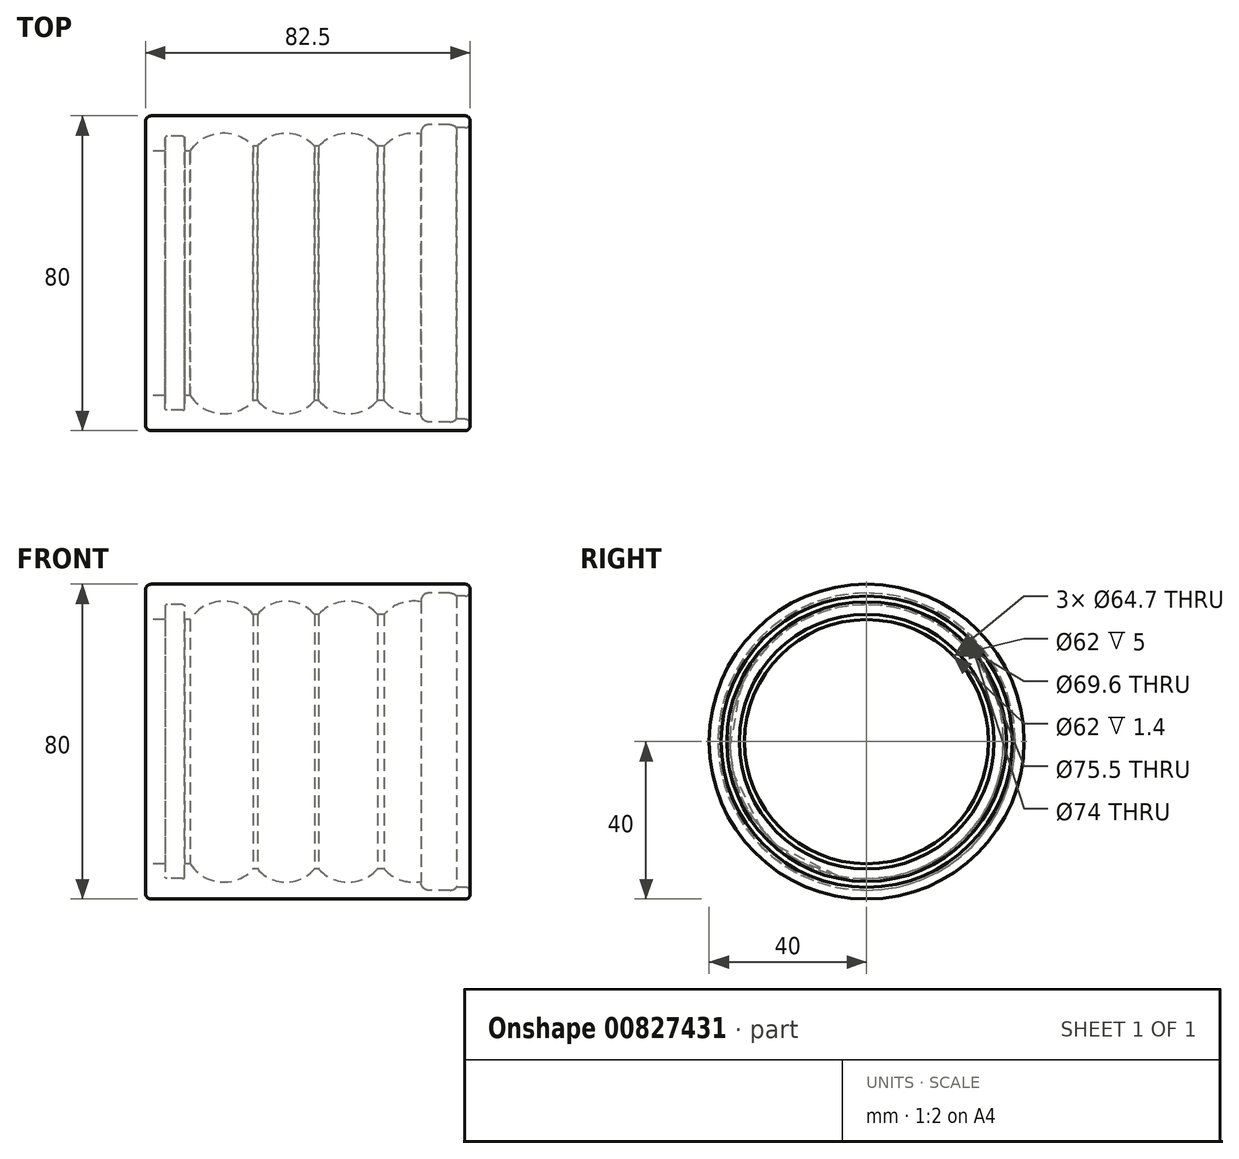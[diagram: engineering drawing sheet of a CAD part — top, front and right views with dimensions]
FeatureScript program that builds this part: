
annotation { "Feature Type Name" : "Feature", "Feature Type Description" : "" }
export const myFeature = defineFeature(function(context is Context, id is Id, definition is map)
    precondition{}
    {
        {
            var Q0;
            Q0=qCreatedBy(makeId("Front.planeOp"),FACE);
            var sketch = newSketch(context, id + "F0", { "sketchPlane" : qUnion([Q0])});
            skLineSegment(sketch, "E0", {"start": v(-106.11, 0) * mm, "end": v(111.06, 0) * mm, "construction": true});
            skLineSegment(sketch, "E1", {"start": v(82.5, 40) * mm, "end": v(0, 40) * mm});
            skLineSegment(sketch, "E2", {"start": v(0, 40) * mm, "end": v(0, 31) * mm});
            skLineSegment(sketch, "E3", {"start": v(0, 31) * mm, "end": v(5, 31) * mm});
            skLineSegment(sketch, "E4", {"start": v(5, 31) * mm, "end": v(5, 34.8) * mm});
            skLineSegment(sketch, "E5", {"start": v(5, 34.8) * mm, "end": v(10, 34.8) * mm});
            skLineSegment(sketch, "E6", {"start": v(27.35, 32.35) * mm, "end": v(28.45, 32.35) * mm});
            skLineSegment(sketch, "E7", {"start": v(70, 35.52) * mm, "end": v(70, 37.75) * mm});
            skLineSegment(sketch, "E8", {"start": v(70, 37.75) * mm, "end": v(79, 37.75) * mm});
            skLineSegment(sketch, "E9", {"start": v(79, 37.75) * mm, "end": v(79, 37) * mm});
            skLineSegment(sketch, "E10", {"start": v(79, 37) * mm, "end": v(82.5, 37) * mm});
            skPoint(sketch, "E11.start.orphan", {"position": v(82.5, 37.75) * mm});
            skLineSegment(sketch, "E12", {"start": v(82.5, 40) * mm, "end": v(82.5, 37) * mm});
            skArc(sketch, "E13", {"start": v(58.97, 32.35) * mm, "mid": v(51.5, 35.7) * mm, "end": v(44.03, 32.35) * mm});
            skArc(sketch, "E14", {"start": v(70, 35.52) * mm, "mid": v(64.92, 35.17) * mm, "end": v(60.67, 32.35) * mm});
            skLineSegment(sketch, "E15", {"start": v(10, 34.8) * mm, "end": v(10, 31) * mm});
            skLineSegment(sketch, "E16", {"start": v(10, 31) * mm, "end": v(11.4, 31) * mm});
            skArc(sketch, "E17.trimOffspring", {"start": v(27.35, 32.35) * mm, "mid": v(19.04, 35.66) * mm, "end": v(11.4, 31) * mm});
            skPoint(sketch, "E18.center.orphan", {"position": v(19.5, 25.7) * mm});
            skLineSegment(sketch, "E19.trimOffspring", {"start": v(42.93, 32.35) * mm, "end": v(44.03, 32.35) * mm});
            skArc(sketch, "E20.trimOffspring", {"start": v(42.93, 32.35) * mm, "mid": v(35.69, 35.7) * mm, "end": v(28.45, 32.35) * mm});
            skPoint(sketch, "E21.center.orphan", {"position": v(35.5, 25.7) * mm});
            skLineSegment(sketch, "E22", {"start": v(-5.4, 35.7) * mm, "end": v(96.54, 35.7) * mm, "construction": true});
            skLineSegment(sketch, "E23.trimOffspring", {"start": v(58.97, 32.35) * mm, "end": v(60.67, 32.35) * mm});
            skSolve(sketch);
        }
        {
            var Q0;
            Q0=makeQuery(id+"F0.imprint","IMPRINT",FACE,{"disambiguationData":[TD([[makeQuery(id+"F0.imprint","IMPRINT",EDGE,{"derivedFrom":sQuery(id+"F0.wireOp",EDGE,"E1")}),1.0]])]});
            var Q1;
            Q1=sQuery(id+"F0.wireOp",EDGE,"E0");
            revolve(context, id + "F1", {"surfaceOperationType" : NewSurfaceOperationType.NEW, "entities" : qUnion([Q0]), "axis" : qUnion([Q1]), "revolveType" : RevolveType.FULL});
        }
        {
            var Q0;
            Q0=makeQuery(id+"F1.opRevolve","SWEPT_EDGE",EDGE,{"disambiguationData":[OSD([sQuery(id+"F0.wireOp",EDGE,"E4"),sQuery(id+"F0.wireOp",EDGE,"E5")])]});
            var Q1;
            Q1=makeQuery(id+"F1.opRevolve","SWEPT_EDGE",EDGE,{"disambiguationData":[OSD([sQuery(id+"F0.wireOp",EDGE,"E5"),sQuery(id+"F0.wireOp",EDGE,"E15")])]});
            fillet(context, id + "F2", {"entities" : qUnion([Q0, Q1]), "radius" : .5 * mm, "tangentPropagation" : true, "allowEdgeOverflow" : false});
        }
        {
            var Q0;
            Q0=makeQuery(id+"F1.opRevolve","SWEPT_EDGE",EDGE,{"disambiguationData":[OSD([sQuery(id+"F0.wireOp",EDGE,"E7"),sQuery(id+"F0.wireOp",EDGE,"E8")])]});
            var Q1;
            Q1=makeQuery(id+"F1.opRevolve","SWEPT_EDGE",EDGE,{"disambiguationData":[OSD([sQuery(id+"F0.wireOp",EDGE,"E8"),sQuery(id+"F0.wireOp",EDGE,"E9")])]});
            fillet(context, id + "F3", {"entities" : qUnion([Q0, Q1]), "radius" : 2 * mm, "tangentPropagation" : true, "allowEdgeOverflow" : false});
        }
        {
            var Q0;
            Q0=makeQuery(id+"F1.opRevolve","SWEPT_EDGE",EDGE,{"disambiguationData":[OSD([sQuery(id+"F0.wireOp",EDGE,"E1"),sQuery(id+"F0.wireOp",EDGE,"E12")])]});
            var Q1;
            Q1=makeQuery(id+"F1.opRevolve","SWEPT_EDGE",EDGE,{"disambiguationData":[OSD([sQuery(id+"F0.wireOp",EDGE,"E10"),sQuery(id+"F0.wireOp",EDGE,"E12")])]});
            fillet(context, id + "F4", {"entities" : qUnion([Q0, Q1]), "radius" : 1.25 * mm, "tangentPropagation" : true, "allowEdgeOverflow" : false});
        }
        {
            var Q0;
            Q0=makeQuery(id+"F1.opRevolve","SWEPT_EDGE",EDGE,{"disambiguationData":[OSD([sQuery(id+"F0.wireOp",EDGE,"E1"),sQuery(id+"F0.wireOp",EDGE,"E2")])]});
            fillet(context, id + "F5", {"entities" : qUnion([Q0]), "radius" : 1.5 * mm, "tangentPropagation" : true, "allowEdgeOverflow" : false});
        }
    });
